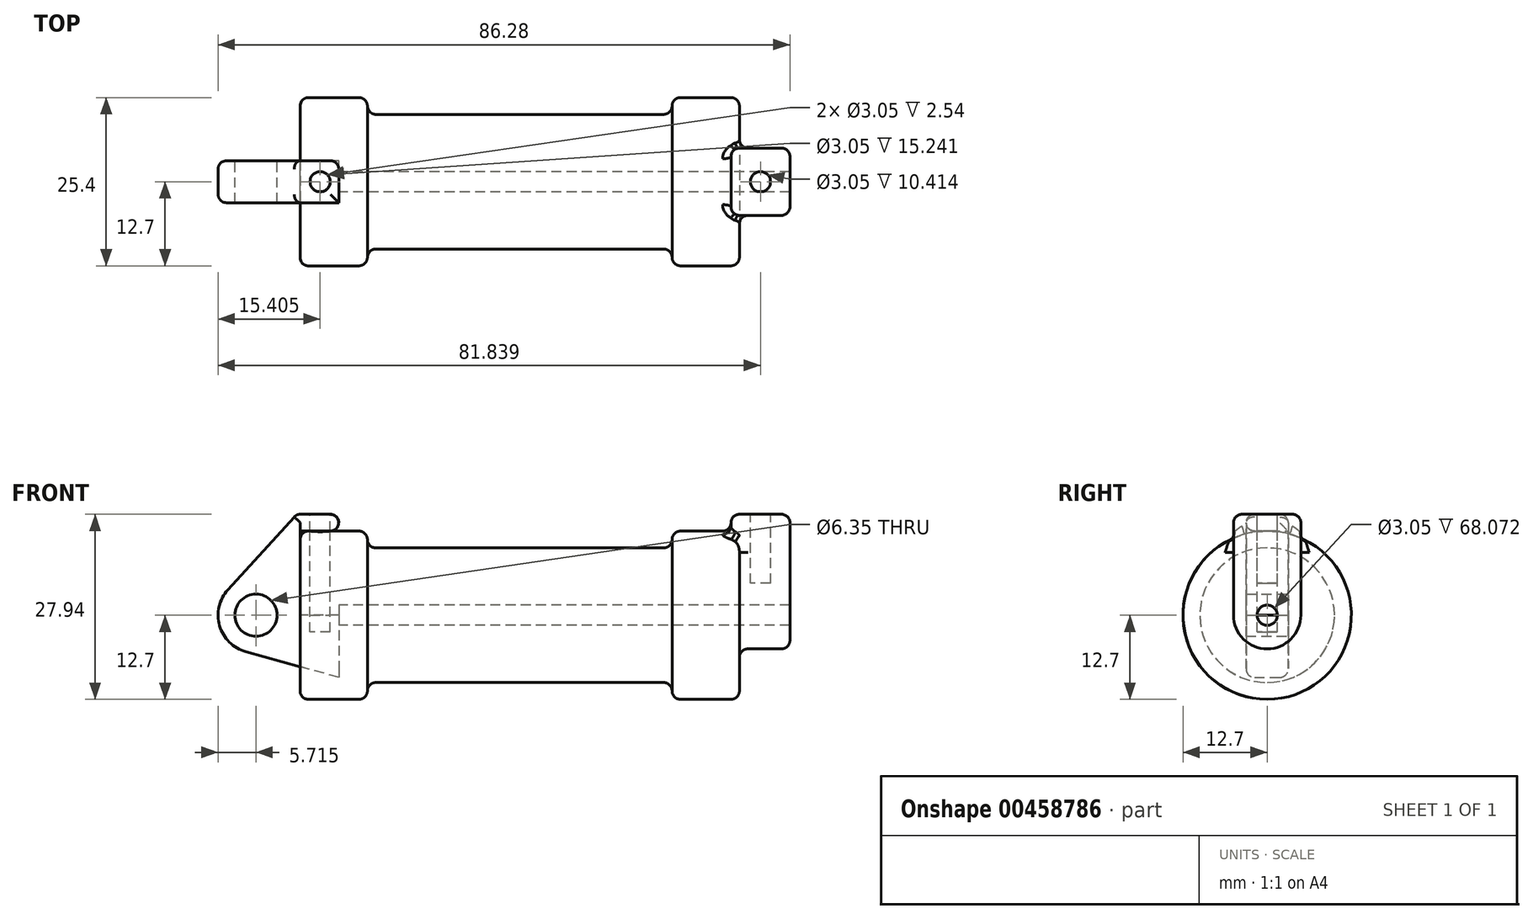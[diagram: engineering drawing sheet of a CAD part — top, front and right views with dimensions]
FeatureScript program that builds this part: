
annotation { "Feature Type Name" : "Feature", "Feature Type Description" : "" }
export const myFeature = defineFeature(function(context is Context, id is Id, definition is map)
    precondition{}
    {
        {
            var Q0;
            Q0=qCreatedBy(makeId("Front.planeOp"),FACE);
            var sketch = newSketch(context, id + "F0", { "sketchPlane" : qUnion([Q0])});
            skLineSegment(sketch, "E0", {"start": v(0, 0) * mm, "end": v(0, 12.7) * mm});
            skLineSegment(sketch, "E1", {"start": v(0, 12.7) * mm, "end": v(10.16, 12.7) * mm});
            skLineSegment(sketch, "E2", {"start": v(10.16, 12.7) * mm, "end": v(10.16, 10.16) * mm});
            skLineSegment(sketch, "E3", {"start": v(10.16, 10.16) * mm, "end": v(56.13, 10.16) * mm});
            skLineSegment(sketch, "E4", {"start": v(56.13, 10.16) * mm, "end": v(56.13, 12.7) * mm});
            skLineSegment(sketch, "E5", {"start": v(56.13, 12.7) * mm, "end": v(66.3, 12.7) * mm});
            skLineSegment(sketch, "E6", {"start": v(66.3, 12.7) * mm, "end": v(66.3, 0) * mm});
            skLineSegment(sketch, "E7", {"start": v(66.3, 0) * mm, "end": v(0, 0) * mm});
            skLineSegment(sketch, "E8", {"start": v(5.84, 15.24) * mm, "end": v(-0.5, 15.24) * mm});
            skLineSegment(sketch, "E9", {"start": v(-0.5, 15.24) * mm, "end": v(-10.88, 3.85) * mm});
            skLineSegment(sketch, "E10", {"start": v(0, 0) * mm, "end": v(-6.65, 0) * mm});
            skCircle(sketch, "E11", {"center": v(-6.65, 0) * mm, "radius": 5.72 * mm});
            skCircle(sketch, "E12", {"center": v(-6.65, 0) * mm, "radius": 3.18 * mm});
            skLineSegment(sketch, "E13", {"start": v(5.84, 15.24) * mm, "end": v(5.84, -9.4) * mm});
            skLineSegment(sketch, "E14", {"start": v(5.84, -9.4) * mm, "end": v(-8.18, -5.5) * mm});
            skSolve(sketch);
        }
        {
            var Q0;
            {var subQ0=sQuery(id+"F0.wireOp",EDGE,"E2");Q0=makeQuery(id+"F0.imprint","IMPRINT",FACE,{"disambiguationData":[TD([[makeQuery(id+"F0.imprint","IMPRINT",EDGE,{"derivedFrom":subQ0}),-1.0]])]});}
            var Q1;
            {var subQ0=sQuery(id+"F0.wireOp",EDGE,"E0");Q1=makeQuery(id+"F0.imprint","IMPRINT",FACE,{"disambiguationData":[TD([[makeQuery(id+"F0.imprint","IMPRINT",EDGE,{"derivedFrom":subQ0}),-1.0]])]});}
            var Q2;
            Q2=sQuery(id+"F0.wireOp",EDGE,"E7");
            revolve(context, id + "F1", {"entities" : qUnion([Q0, Q1]), "axis" : qUnion([Q2]), "revolveType" : RevolveType.FULL});
        }
        {
            var Q0;
            {var subQ1=sQuery(id+"F0.wireOp",EDGE,"E0");Q0=makeQuery(id+"F0.imprint","IMPRINT",FACE,{"disambiguationData":[TD([[makeQuery(id+"F0.imprint","IMPRINT",EDGE,{"derivedFrom":subQ1}),1.0]])]});}
            var Q1;
            {var subQ5=sQuery(id+"F0.wireOp",EDGE,"E12");Q1=makeQuery(id+"F0.imprint","IMPRINT",FACE,{"disambiguationData":[TD([[makeQuery(id+"F0.imprint","IMPRINT",EDGE,{"derivedFrom":subQ5}),-1.0]])]});}
            var Q2;
            {var subQ0=sQuery(id+"F0.wireOp",EDGE,"E14");Q2=makeQuery(id+"F0.imprint","IMPRINT",FACE,{"disambiguationData":[TD([[makeQuery(id+"F0.imprint","IMPRINT",EDGE,{"derivedFrom":subQ0}),-1.0]])]});}
            extrude(context, id + "F2", {"entities" : qUnion([Q0, Q1, Q2]), "depth" : 6.35 * mm, "symmetric" : true});
        }
        {
            var Q0;
            Q0=makeQuery(id+"F1.opRevolve","SWEPT_FACE",FACE,{"disambiguationData":[OSD([sQuery(id+"F0.wireOp",EDGE,"E6")])]});
            var sketch = newSketch(context, id + "F3", { "sketchPlane" : qUnion([Q0])});
            skCircle(sketch, "E15", {"center": v(0, 0) * mm, "radius": 5.08 * mm});
            skCircle(sketch, "E16", {"center": v(0, 0) * mm, "radius": 1.52 * mm});
            skLineSegment(sketch, "E17", {"start": v(5.08, 0) * mm, "end": v(5.08, 15.24) * mm});
            skLineSegment(sketch, "E18", {"start": v(-5.08, 0) * mm, "end": v(-5.08, 15.24) * mm});
            skLineSegment(sketch, "E19", {"start": v(-5.08, 15.24) * mm, "end": v(5.08, 15.24) * mm});
            skSolve(sketch);
        }
        {
            var Q0;
            Q0 = qSketchRegion(id + "F3", true);
            extrude(context, id + "F4", {"entities" : qUnion([Q0]), "operationType" : NewBodyOperationType.ADD, "depth" : 7.62 * mm, "hasSecondDirection" : true, "secondDirectionOppositeDirection" : true, "secondDirectionDepth" : 1.27 * mm});
        }
        {
            var Q0;
            Q0=makeQuery(id+"F4.boolean.opBoolean","SPLIT",FACE,{"disambiguationData":[TD([makeQuery(id+"F4.opExtrude","SWEPT_FACE",FACE,{"disambiguationData":[OSD([sQuery(id+"F3.wireOp",EDGE,"E16")])]})])],"derivedFrom":makeQuery(id+"F1.opRevolve","SWEPT_FACE",FACE,{"disambiguationData":[OSD([sQuery(id+"F0.wireOp",EDGE,"E6")])]})});
            extrude(context, id + "F5", {"entities" : qUnion([Q0]), "operationType" : NewBodyOperationType.REMOVE, "oppositeDirection" : true, "depth" : 60.45 * mm});
        }
        {
            var Q0;
            Q0=makeQuery(id+"F2.opExtrude","SWEPT_FACE",FACE,{"disambiguationData":[OSD([sQuery(id+"F0.wireOp",EDGE,"E8")])]});
            var sketch = newSketch(context, id + "F6", { "sketchPlane" : qUnion([Q0])});
            skCircle(sketch, "E20", {"center": v(3.03, 0) * mm, "radius": 1.52 * mm});
            skSolve(sketch);
        }
        {
            var Q0;
            Q0 = qSketchRegion(id + "F6", true);
            extrude(context, id + "F7", {"entities" : qUnion([Q0]), "operationType" : NewBodyOperationType.REMOVE, "oppositeDirection" : true, "depth" : 17.78 * mm});
        }
        {
            var Q0;
            Q0=makeQuery(id+"F4.opExtrude","SWEPT_FACE",FACE,{"disambiguationData":[OSD([sQuery(id+"F3.wireOp",EDGE,"E19")])]});
            var sketch = newSketch(context, id + "F8", { "sketchPlane" : qUnion([Q0])});
            skCircle(sketch, "E21", {"center": v(69.47, 0) * mm, "radius": 1.52 * mm});
            skSolve(sketch);
        }
        {
            var Q0;
            Q0 = qSketchRegion(id + "F8", true);
            extrude(context, id + "F9", {"entities" : qUnion([Q0]), "operationType" : NewBodyOperationType.REMOVE, "oppositeDirection" : true, "depth" : 10.4 * mm});
        }
        {
            var Q0;
            Q0=makeQuery(id+"F1.opRevolve","SWEPT_EDGE",EDGE,{"disambiguationData":[OSD([sQuery(id+"F0.wireOp",EDGE,"E2"),sQuery(id+"F0.wireOp",EDGE,"E3")])]});
            var Q1;
            Q1=makeQuery(id+"F1.opRevolve","SWEPT_EDGE",EDGE,{"disambiguationData":[OSD([sQuery(id+"F0.wireOp",EDGE,"E1"),sQuery(id+"F0.wireOp",EDGE,"E2")])]});
            fillet(context, id + "F10", {"entities" : qUnion([Q0, Q1]), "radius" : 1.27 * mm, "tangentPropagation" : true, "allowEdgeOverflow" : false});
        }
        {
            var Q0;
            Q0=makeQuery(id+"F1.opRevolve","SWEPT_EDGE",EDGE,{"disambiguationData":[OSD([sQuery(id+"F0.wireOp",EDGE,"E3"),sQuery(id+"F0.wireOp",EDGE,"E4")])]});
            var Q1;
            Q1=makeQuery(id+"F1.opRevolve","SWEPT_EDGE",EDGE,{"disambiguationData":[OSD([sQuery(id+"F0.wireOp",EDGE,"E4"),sQuery(id+"F0.wireOp",EDGE,"E5")])]});
            var Q2;
            Q2=makeQuery(id+"F1.opRevolve","SWEPT_EDGE",EDGE,{"disambiguationData":[OSD([sQuery(id+"F0.wireOp",EDGE,"E5"),sQuery(id+"F0.wireOp",EDGE,"E6")])]});
            fillet(context, id + "F11", {"entities" : qUnion([Q0, Q1, Q2]), "radius" : 1.27 * mm, "tangentPropagation" : true, "allowEdgeOverflow" : false});
        }
        {
            var Q0;
            Q0=makeQuery(id+"F4.opExtrude","CAP_EDGE",EDGE,{"disambiguationData":[OSD([sQuery(id+"F3.wireOp",EDGE,"E18")])],"isStart":true});
            var Q1;
            Q1=makeQuery(id+"F4.opExtrude","SWEPT_EDGE",EDGE,{"disambiguationData":[OSD([sQuery(id+"F3.wireOp",EDGE,"E17"),sQuery(id+"F3.wireOp",EDGE,"E19")])]});
            var Q2;
            Q2=makeQuery(id+"F4.opExtrude","CAP_EDGE",EDGE,{"disambiguationData":[OSD([sQuery(id+"F3.wireOp",EDGE,"E19")])],"isStart":true});
            var Q3;
            Q3=makeQuery(id+"F4.opExtrude","CAP_EDGE",EDGE,{"disambiguationData":[OSD([sQuery(id+"F3.wireOp",EDGE,"E17")])],"isStart":true});
            var Q4;
            Q4=makeQuery(id+"F4.opExtrude","SWEPT_EDGE",EDGE,{"disambiguationData":[OSD([sQuery(id+"F3.wireOp",EDGE,"E18"),sQuery(id+"F3.wireOp",EDGE,"E19")])]});
            var Q5;
            Q5=makeQuery(id+"F4.opExtrude","CAP_EDGE",EDGE,{"disambiguationData":[OSD([sQuery(id+"F3.wireOp",EDGE,"E19")])],"isStart":false});
            var Q6;
            Q6=makeQuery(id+"F4.opExtrude","CAP_EDGE",EDGE,{"disambiguationData":[OSD([sQuery(id+"F3.wireOp",EDGE,"E18")])],"isStart":false});
            fillet(context, id + "F12", {"entities" : qUnion([Q0, Q1, Q2, Q3, Q4, Q5, Q6]), "radius" : 1.27 * mm, "tangentPropagation" : true, "allowEdgeOverflow" : false});
        }
        {
            var Q0;
            Q0=makeQuery(id+"F4.boolean.opBoolean","INTERSECT",EDGE,{"derivedFrom":[makeQuery(id+"F1.opRevolve","SWEPT_FACE",FACE,{"disambiguationData":[OSD([sQuery(id+"F0.wireOp",EDGE,"E6")])]}),makeQuery(id+"F4.opExtrude","SWEPT_FACE",FACE,{"disambiguationData":[OSD([sQuery(id+"F3.wireOp",EDGE,"E18")])]})]});
            var Q1;
            Q1=makeQuery(id+"F2.opExtrude","CAP_EDGE",EDGE,{"disambiguationData":[OSD([sQuery(id+"F0.wireOp",EDGE,"E9")])],"isStart":true});
            var Q2;
            Q2=makeQuery(id+"F2.opExtrude","CAP_EDGE",EDGE,{"disambiguationData":[OSD([sQuery(id+"F0.wireOp",EDGE,"E9")])],"isStart":false});
            var Q3;
            Q3=makeQuery(id+"F2.opExtrude","CAP_EDGE",EDGE,{"disambiguationData":[OSD([sQuery(id+"F0.wireOp",EDGE,"E8")])],"isStart":true});
            fillet(context, id + "F13", {"entities" : qUnion([Q0, Q1, Q2, Q3]), "radius" : 1.27 * mm, "tangentPropagation" : true, "allowEdgeOverflow" : false});
        }
        {
            var Q0;
            Q0=makeQuery(id+"F1.opRevolve","SWEPT_EDGE",EDGE,{"disambiguationData":[OSD([sQuery(id+"F0.wireOp",EDGE,"E0"),sQuery(id+"F0.wireOp",EDGE,"E1")])]});
            var Q1;
            Q1=makeQuery(id+"F2.opExtrude","SWEPT_EDGE",EDGE,{"disambiguationData":[OSD([sQuery(id+"F0.wireOp",EDGE,"E8"),sQuery(id+"F0.wireOp",EDGE,"E13")])]});
            var Q2;
            Q2=makeQuery(id+"F2.opExtrude","CAP_EDGE",EDGE,{"disambiguationData":[OSD([sQuery(id+"F0.wireOp",EDGE,"E8")])],"isStart":false});
            var Q3;
            Q3=makeQuery(id+"F2.opExtrude","CAP_EDGE",EDGE,{"disambiguationData":[OSD([sQuery(id+"F0.wireOp",EDGE,"E1")])],"isStart":false});
            var Q4;
            Q4=makeQuery(id+"F2.opExtrude","SWEPT_EDGE",EDGE,{"disambiguationData":[OSD([sQuery(id+"F0.wireOp",EDGE,"E1"),sQuery(id+"F0.wireOp",EDGE,"E13")])]});
            fillet(context, id + "F14", {"entities" : qUnion([Q0, Q1, Q2, Q3, Q4]), "radius" : 1.27 * mm, "tangentPropagation" : true, "allowEdgeOverflow" : false});
        }
    });
